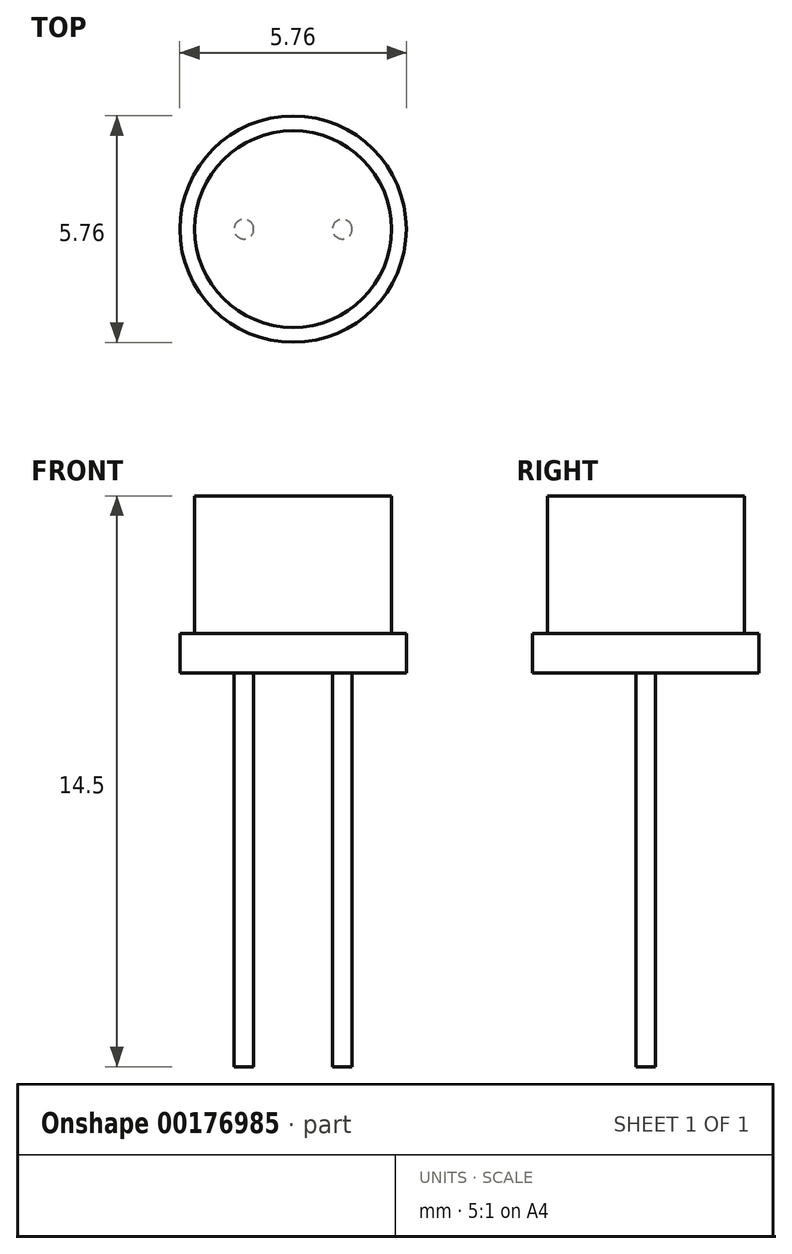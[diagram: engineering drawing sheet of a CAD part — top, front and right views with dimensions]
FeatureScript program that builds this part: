
annotation { "Feature Type Name" : "Feature", "Feature Type Description" : "" }
export const myFeature = defineFeature(function(context is Context, id is Id, definition is map)
    precondition{}
    {
        {
            var Q0;
            Q0=qCreatedBy(makeId("Top.planeOp"),FACE);
            var sketch = newSketch(context, id + "F0", { "sketchPlane" : qUnion([Q0])});
            skCircle(sketch, "E0", {"center": v(0, 0) * mm, "radius": 2.5 * mm});
            skCircle(sketch, "E1", {"center": v(0, 0) * mm, "radius": 2.88 * mm});
            skCircle(sketch, "E2", {"center": v(-1.25, 0) * mm, "radius": 0.25 * mm});
            skCircle(sketch, "E3", {"center": v(1.25, 0) * mm, "radius": 0.25 * mm});
            skSolve(sketch);
        }
        {
            var Q0;
            Q0=makeQuery(id+"F0.imprint","IMPRINT",FACE,{"disambiguationData":[TD([[makeQuery(id+"F0.imprint","IMPRINT",EDGE,{"derivedFrom":sQuery(id+"F0.wireOp",EDGE,"E0")}),1.0]])]});
            var Q1;
            Q1=makeQuery(id+"F0.imprint","IMPRINT",FACE,{"disambiguationData":[TD([[makeQuery(id+"F0.imprint","IMPRINT",EDGE,{"derivedFrom":sQuery(id+"F0.wireOp",EDGE,"E2")}),1.0]])]});
            var Q2;
            Q2=makeQuery(id+"F0.imprint","IMPRINT",FACE,{"disambiguationData":[TD([[makeQuery(id+"F0.imprint","IMPRINT",EDGE,{"derivedFrom":sQuery(id+"F0.wireOp",EDGE,"E3")}),1.0]])]});
            extrude(context, id + "F1", {"entities" : qUnion([Q0, Q1, Q2]), "depth" : 4.5 * mm, "offsetDistance" : 25 * mm});
        }
        {
            var Q0;
            Q0=makeQuery(id+"F0.imprint","IMPRINT",FACE,{"disambiguationData":[TD([[makeQuery(id+"F0.imprint","IMPRINT",EDGE,{"derivedFrom":sQuery(id+"F0.wireOp",EDGE,"E0")}),-1.0]])]});
            extrude(context, id + "F2", {"entities" : qUnion([Q0]), "operationType" : NewBodyOperationType.ADD, "depth" : 1 * mm, "offsetDistance" : 25 * mm});
        }
        {
            var Q0;
            Q0=makeQuery(id+"F0.imprint","IMPRINT",FACE,{"disambiguationData":[TD([[makeQuery(id+"F0.imprint","IMPRINT",EDGE,{"derivedFrom":sQuery(id+"F0.wireOp",EDGE,"E2")}),1.0]])]});
            var Q1;
            Q1=makeQuery(id+"F0.imprint","IMPRINT",FACE,{"disambiguationData":[TD([[makeQuery(id+"F0.imprint","IMPRINT",EDGE,{"derivedFrom":sQuery(id+"F0.wireOp",EDGE,"E3")}),1.0]])]});
            extrude(context, id + "F3", {"entities" : qUnion([Q0, Q1]), "operationType" : NewBodyOperationType.ADD, "oppositeDirection" : true, "depth" : 10 * mm, "offsetDistance" : 25 * mm});
        }
    });
